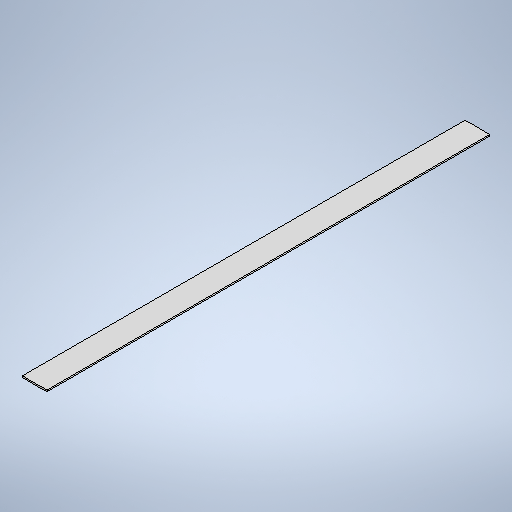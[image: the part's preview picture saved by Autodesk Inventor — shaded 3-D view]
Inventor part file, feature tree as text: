
AUTODESK INVENTOR PART (.ipt)
format: ipt  version: 2025 (Build 290162010, 162A)  size: 260,608 bytes
history: native  units: mm
features: sheet_metal_op x1, sketch x1, other x1
ambient origin geometry x8: Origin, YZ Plane, XZ Plane, XY Plane, X Axis, Y Axis, Z Axis, Center Point
bodies: Body1 (feature_tree)
feature tree (3):
  sheet_metal_op  "Face2"
  sketch  "Sketch1"  dims[d11=1100.0mm d12=900.0mm d13=25.0mm d14=25.0mm d15=3.0mm]
  other  "Plate2"
